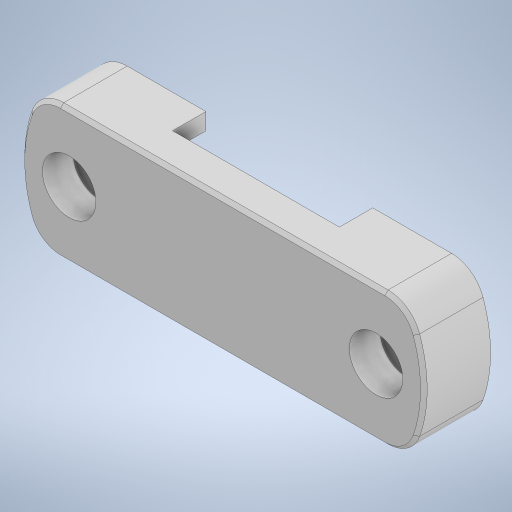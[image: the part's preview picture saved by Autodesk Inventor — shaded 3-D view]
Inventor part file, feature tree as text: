
AUTODESK INVENTOR PART (.ipt)
format: ipt  version: 2023 (Build 270158000, 158)  size: 304,128 bytes
history: native  units: mm
features: sketch x5, projected_geometry x5, extrude x4, other x1, hole x1, fillet x1, chamfer x1
ambient origin geometry x8: Origin, YZ Plane, XZ Plane, XY Plane, X Axis, Y Axis, Z Axis, Center Point
bodies: Body1 (feature_tree)
feature tree (18):
  other  "Těleso1"
  extrude  "Vysunutí1"  Depth=35.0mm
  extrude  "Vysunutí2"  Depth=20.0mm
  extrude  "Vysunutí3"  Depth=10.0mm TaperAngle=0.0deg
  extrude  "Vysunutí4"  Depth=15.0mm
  hole  "Díra1"  [1 undecoded]
  fillet  "Zaoblení2"  Radius=7.5mm
  chamfer  "Zkosení1"  Distance=5.0mm
  sketch  "Náčrt1"
  sketch  "Náčrt2"
  projected_geometry  "Promítnutá smyčka1"
  sketch  "Náčrt3"
  projected_geometry  "Promítnutá smyčka2"
  sketch  "Náčrt4"
  projected_geometry  "Promítnutá smyčka3"
  projected_geometry  "Promítnutá smyčka4"
  sketch  "Náčrt5"
  projected_geometry  "Promítnutá smyčka5"
note: 1 required parameter value undecoded (feature->parameter linkage not recoverable at this tier; creation-order binding heuristic only, values carry confidence <= 0.55)
